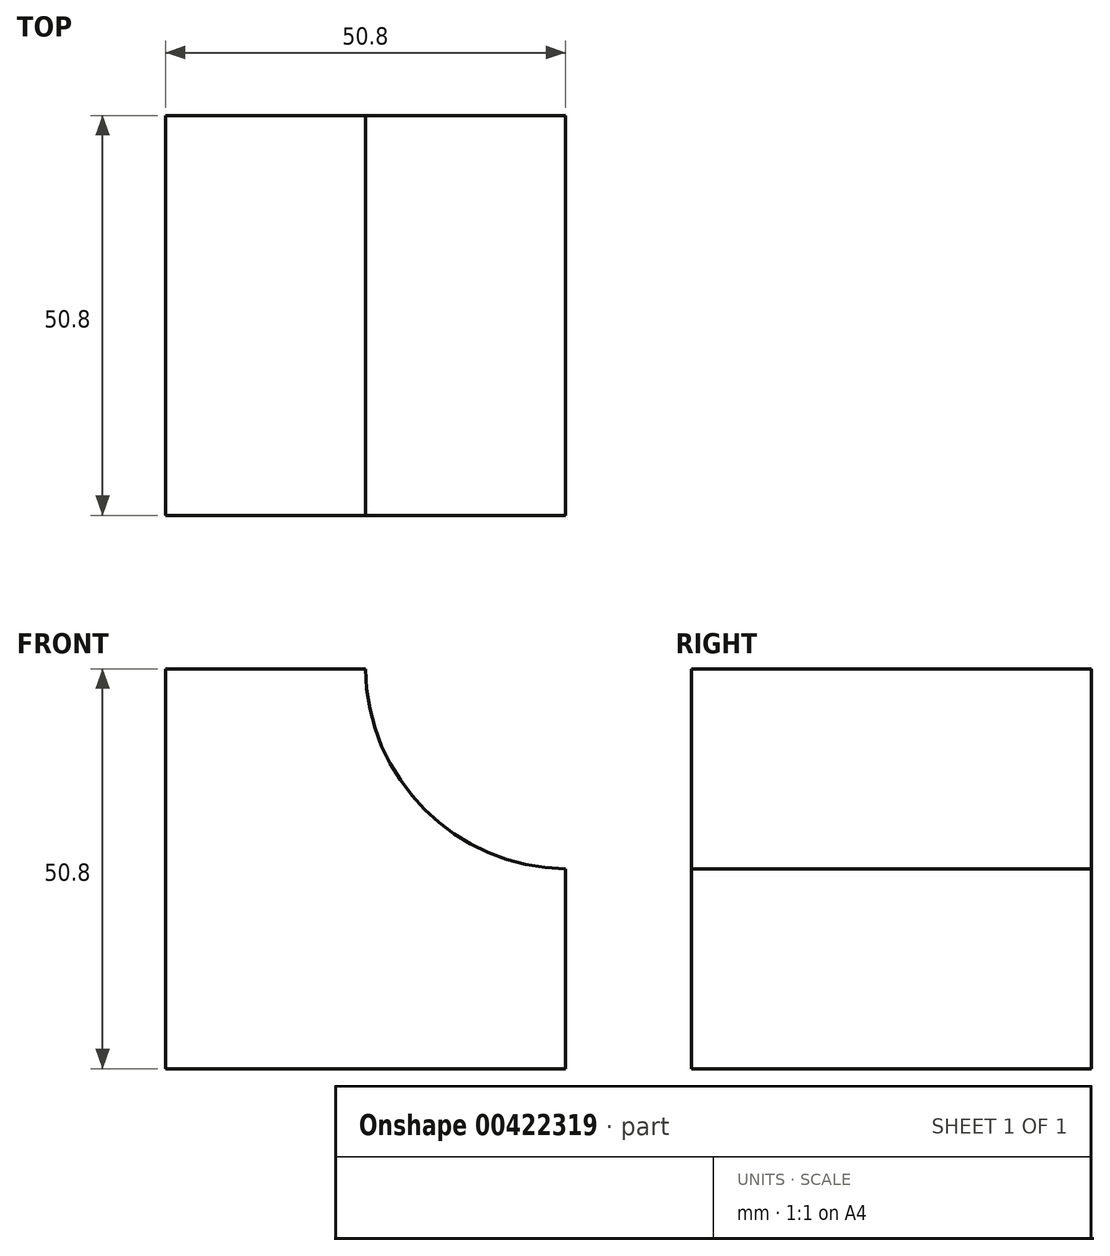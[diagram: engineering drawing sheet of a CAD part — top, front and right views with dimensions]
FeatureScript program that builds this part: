
annotation { "Feature Type Name" : "Feature", "Feature Type Description" : "" }
export const myFeature = defineFeature(function(context is Context, id is Id, definition is map)
    precondition{}
    {
        {
            var Q0;
            Q0=qCreatedBy(makeId("Front.planeOp"),FACE);
            var sketch = newSketch(context, id + "F0", { "sketchPlane" : qUnion([Q0])});
            skLineSegment(sketch, "E0", {"start": v(0, 50.8) * mm, "end": v(25.4, 50.8) * mm});
            skLineSegment(sketch, "E1", {"start": v(0, 50.8) * mm, "end": v(0, 0) * mm});
            skLineSegment(sketch, "E2", {"start": v(0, 0) * mm, "end": v(50.8, 0) * mm});
            skLineSegment(sketch, "E3", {"start": v(50.8, 0) * mm, "end": v(50.8, 25.4) * mm});
            skArc(sketch, "E4", {"start": v(25.4, 50.8) * mm, "mid": v(32.91, 32.91) * mm, "end": v(50.8, 25.4) * mm});
            skSolve(sketch);
        }
        {
            var Q0;
            Q0=makeQuery(id+"F0.imprint","IMPRINT",FACE,{"disambiguationData":[TD([[makeQuery(id+"F0.imprint","IMPRINT",EDGE,{"derivedFrom":sQuery(id+"F0.wireOp",EDGE,"E0")}),-1.0]])]});
            extrude(context, id + "F1", {"entities" : qUnion([Q0]), "depth" : 50.8 * mm});
        }
    });
